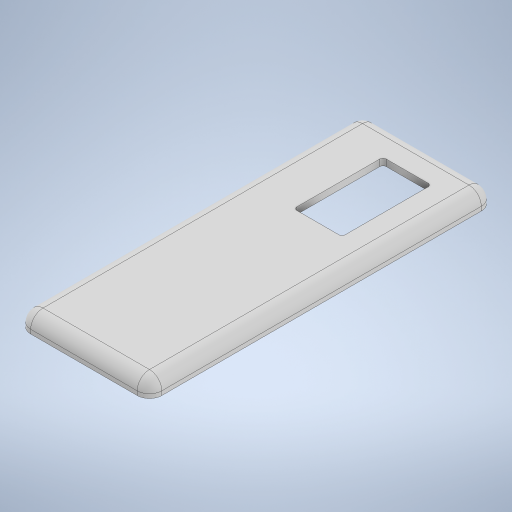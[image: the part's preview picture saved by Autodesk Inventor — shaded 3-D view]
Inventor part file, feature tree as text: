
AUTODESK INVENTOR PART (.ipt)
format: ipt  version: 2023 (Build 270158000, 158)  size: 659,456 bytes
history: native  units: in
note: dims shown in document units (in); Inventor stores cm internally (conversion verified against a paired STEP export)
features: sketch x11, extrude x9, fillet x6, chamfer x5, hole x2, pattern_linear x2, thicken_offset x2, projected_geometry x2, shell x1, plane x1, mirror x1
ambient origin geometry x8: Origin, YZ Plane, XZ Plane, XY Plane, X Axis, Y Axis, Z Axis, Center Point
bodies: Solid1 (feature_tree)
feature tree (42):
  extrude  "Extrusion1"  Depth=6.2992in
  shell  "Shell1"  Thickness=0.7874in
  extrude  "Extrusion2"  Depth=0.9055in
  hole  "Hole1"  [1 undecoded]
  extrude  "Extrusion5"  Depth=0.5906in
  fillet  "Fillet1"  Radius=0.5906in
  fillet  "Fillet2"  Radius=0.5906in
  extrude  "Extrusion3"  Depth=0.1181in
  chamfer  "Chamfer1"  Distance=0.0787in
  chamfer  "Chamfer2"  Distance=0.0787in Angle=45.0deg
  chamfer  "Chamfer3"  Distance=0.0394in Angle=60.0deg
  chamfer  "Chamfer4"  Distance=0.0394in Angle=60.0deg
  chamfer  "Chamfer5"  Distance=0.0394in Angle=60.0deg
  extrude  "Extrusion11"  Depth=0.1969in
  extrude  "Extrusion13"  Depth=5.7087in
  hole  "Hole3"  [1 undecoded]
  extrude  "Extrusion14"  Depth=0.0787in TaperAngle=0.0deg
  fillet  "Fillet5"  Radius=0.315in
  fillet  "Fillet6"  [1 undecoded]
  fillet  "Fillet7"  Radius=0.1181in
  extrude  "Extrusion15"  Depth=0.1575in
  fillet  "Fillet8"  Radius=0.0787in
  extrude  "Extrusion16"  Depth=0.0787in TaperAngle=0.0deg
  plane  "Work Plane6"
  mirror  "Mirror5"
  pattern_linear  "Rectangular Pattern6"  Spacing1=0.0787in  [1 undecoded]
  thicken_offset  "Thicken38"
  thicken_offset  "Thicken39"
  pattern_linear  "Rectangular Pattern7"  Spacing1=0.1575in  [1 undecoded]
  sketch  "Sketch1"  dims[d1=16.5354in d2=6.2992in d3=0.7874in d4=0.0in]
  sketch  "Sketch2"  dims[d5=0.3937in d6=0.9055in]
  sketch  "Sketch3"  dims[d7=0.0in d8=0.0in]
  sketch  "Sketch4"  dims[d13=0.3976in d14=0.2362in d15=0.1575in d16=0.0787in d17=90.0deg d18=0.3937in d19=0.0in d20=0.5906in]
  sketch  "Sketch7"  dims[d21=0.1969in d22=0.5906in d23=0.5906in d24=0.5906in]
  sketch  "Sketch15"  dims[d25=0.5906in d26=0.1181in]
  sketch  "Sketch18"  dims[d27=0.2756in d28=0.0787in d29=0.0in d30=0.0197in d31=0.0787in d32=45.0deg d33=0.0394in d34=0.0787in d35=60.0deg d36=0.0394in d37=0.0787in d38=60.0deg d39=0.0394in d40=0.0787in d41=60.0deg]
  sketch  "Sketch19"  dims[d42=0.0394in d43=0.0787in d44=60.0deg d51=0.1969in]
  projected_geometry  "Projected Loop2"
  sketch  "Sketch20"  dims[d52=0.3937in d53=0.0in d89=5.7087in]
  projected_geometry  "Projected Loop3"
  sketch  "Sketch21"  dims[d99=0.5906in d100=0.5906in]
  sketch  "Sketch22"  dims[d101=0.3937in d102=0.0787in d103=0.0in d115=0.315in d116=0.0in d117=0.0in d118=0.1181in d119=0.0968in d120=0.1969in d121=0.1575in d122=0.0787in d123=90.0deg d124=0.2362in d125=0.8108in d126=0.1575in d127=0.0787in d128=0.0787in d129=0.0in d130=0.0787in d131=0.1575in d132=0.1575in d207=2.9528in d208=0.5906in d209=0.1969in d211=0.3937in d212=0.0in d213=0.0787in d218=0.1575in d219=0.1181in d220=0.0787in d221=0.0787in d222=3.937in d223=0.0in d224=1.1811in d226=1.7717in d227=3.937in d228=3.937in d229=3.937in d230=3.937in d231=0.5512in d232=1.1811in d234=1.7717in d235=0.0787in d236=0.0787in d54=0.0197in d55=0.0344in d78=0.0197in d79=0.0344in d80=0.0197in d81=0.0344in]
note: 5 required parameter values undecoded (feature->parameter linkage not recoverable at this tier; creation-order binding heuristic only, values carry confidence <= 0.55)
